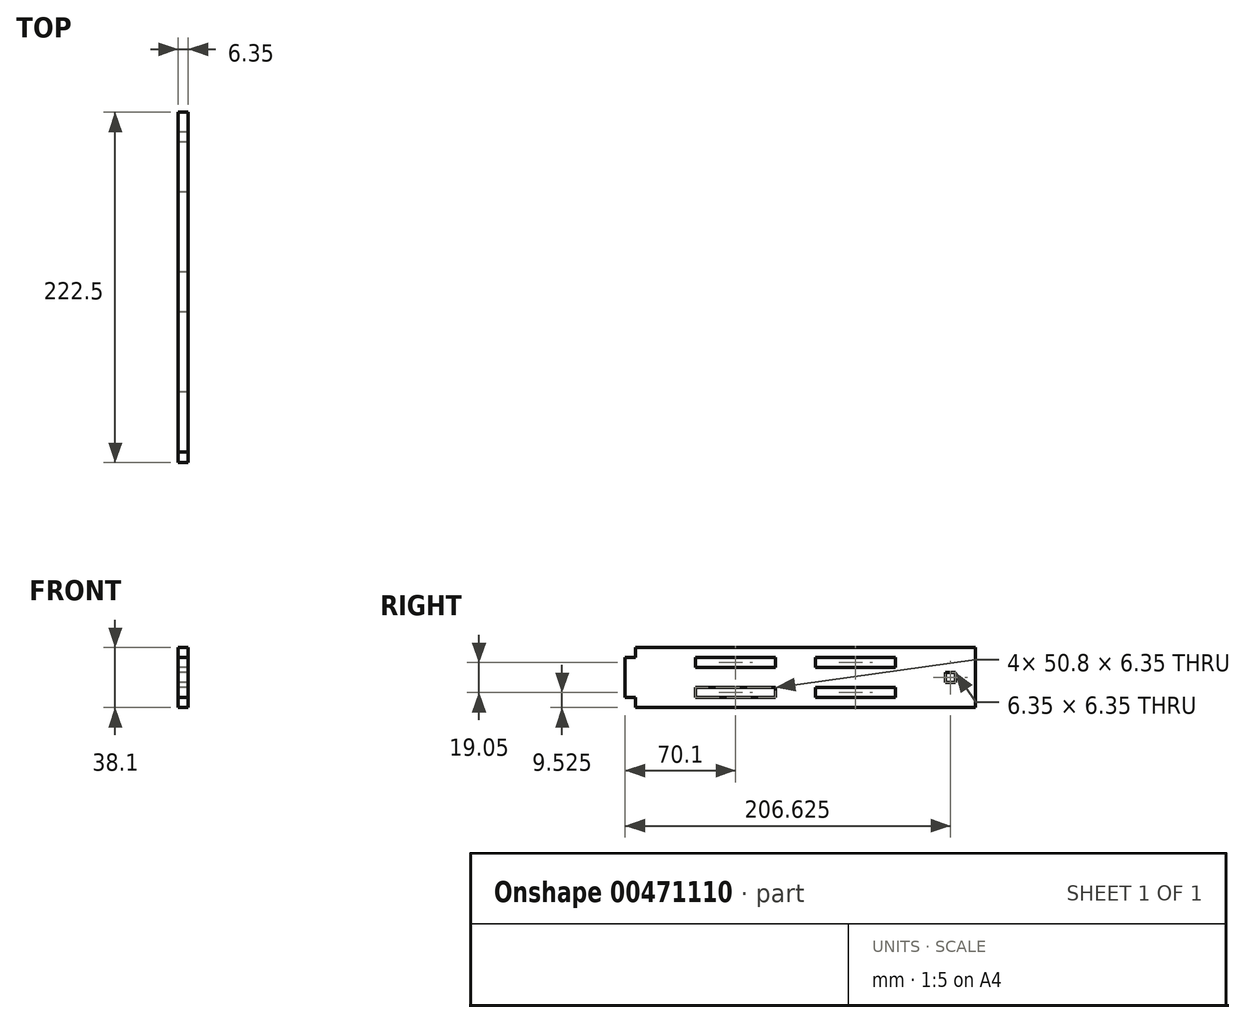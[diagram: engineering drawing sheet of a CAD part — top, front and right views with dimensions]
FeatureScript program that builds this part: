
annotation { "Feature Type Name" : "Feature", "Feature Type Description" : "" }
export const myFeature = defineFeature(function(context is Context, id is Id, definition is map)
    precondition{}
    {
        {
            var Q0;
            Q0=qCreatedBy(makeId("Right.planeOp"),FACE);
            var sketch = newSketch(context, id + "F0", { "sketchPlane" : qUnion([Q0])});
            skLineSegment(sketch, "E0", {"start": v(0, 0) * mm, "end": v(215.9, 0) * mm});
            skLineSegment(sketch, "E1", {"start": v(0, 0) * mm, "end": v(0, -6.35) * mm});
            skLineSegment(sketch, "E2", {"start": v(0, -38.1) * mm, "end": v(215.9, -38.1) * mm});
            skLineSegment(sketch, "E3", {"start": v(215.9, -38.1) * mm, "end": v(215.9, 0) * mm});
            skLineSegment(sketch, "E4", {"start": v(0, -6.35) * mm, "end": v(-6.6, -6.35) * mm});
            skLineSegment(sketch, "E5.MirrorCS", {"start": v(0, -31.75) * mm, "end": v(-6.6, -31.75) * mm});
            skLineSegment(sketch, "E6", {"start": v(-6.6, -31.75) * mm, "end": v(-6.6, -6.35) * mm});
            skLineSegment(sketch, "E7.trimOffspring", {"start": v(0, -31.75) * mm, "end": v(0, -38.1) * mm});
            skLineSegment(sketch, "E8", {"start": v(38.1, -6.35) * mm, "end": v(38.1, -12.7) * mm});
            skLineSegment(sketch, "E9", {"start": v(38.1, -12.7) * mm, "end": v(88.9, -12.7) * mm});
            skLineSegment(sketch, "E10", {"start": v(88.9, -12.7) * mm, "end": v(88.9, -6.35) * mm});
            skLineSegment(sketch, "E11", {"start": v(88.9, -6.35) * mm, "end": v(38.1, -6.35) * mm});
            skLineSegment(sketch, "E12.MirrorCS", {"start": v(114.3, -12.7) * mm, "end": v(114.3, -6.35) * mm});
            skLineSegment(sketch, "E13.MirrorCS", {"start": v(165.1, -12.7) * mm, "end": v(114.3, -12.7) * mm});
            skLineSegment(sketch, "E14.MirrorCS", {"start": v(165.1, -6.35) * mm, "end": v(165.1, -12.7) * mm});
            skLineSegment(sketch, "E15.MirrorCS", {"start": v(88.9, -25.4) * mm, "end": v(88.9, -31.75) * mm});
            skLineSegment(sketch, "E16.MirrorCS", {"start": v(114.3, -25.4) * mm, "end": v(114.3, -31.75) * mm});
            skLineSegment(sketch, "E17.MirrorCS", {"start": v(165.1, -31.75) * mm, "end": v(165.1, -25.4) * mm});
            skLineSegment(sketch, "E18.MirrorCS", {"start": v(38.1, -31.75) * mm, "end": v(38.1, -25.4) * mm});
            skLineSegment(sketch, "E19.MirrorCS", {"start": v(38.1, -25.4) * mm, "end": v(88.9, -25.4) * mm});
            skLineSegment(sketch, "E20.MirrorCS", {"start": v(114.3, -31.75) * mm, "end": v(165.1, -31.75) * mm});
            skLineSegment(sketch, "E21.MirrorCS", {"start": v(165.1, -25.4) * mm, "end": v(114.3, -25.4) * mm});
            skLineSegment(sketch, "E22.MirrorCS", {"start": v(88.9, -31.75) * mm, "end": v(38.1, -31.75) * mm});
            skPoint(sketch, "E23.startSnap0", {"position": v(-6.6, -19.05) * mm});
            skLineSegment(sketch, "E24", {"start": v(114.3, -6.35) * mm, "end": v(165.1, -6.35) * mm});
            skLineSegment(sketch, "E25", {"start": v(203.2, -22.22) * mm, "end": v(196.85, -22.22) * mm});
            skLineSegment(sketch, "E26.MirrorCS", {"start": v(203.2, -15.88) * mm, "end": v(196.85, -15.88) * mm});
            skLineSegment(sketch, "E27", {"start": v(196.85, -15.88) * mm, "end": v(196.85, -22.22) * mm});
            skLineSegment(sketch, "E28", {"start": v(203.2, -15.88) * mm, "end": v(203.2, -22.22) * mm});
            skSolve(sketch);
        }
        {
            var Q0;
            Q0=makeQuery(id+"F0.imprint","IMPRINT",FACE,{"disambiguationData":[TD([[makeQuery(id+"F0.imprint","IMPRINT",EDGE,{"derivedFrom":sQuery(id+"F0.wireOp",EDGE,"E0")}),-1.0]])]});
            extrude(context, id + "F1", {"entities" : qUnion([Q0]), "depth" : 6.35 * mm});
        }
    });
